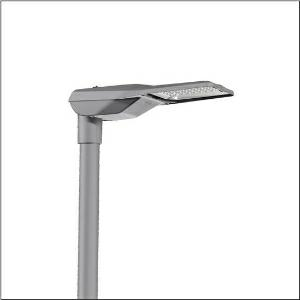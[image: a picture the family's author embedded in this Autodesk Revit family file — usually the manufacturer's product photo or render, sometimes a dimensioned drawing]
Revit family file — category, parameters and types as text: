
# Revit family: streetlight_sl_21_iq_mini___st1_0ab_5xe2m31v08jb_8772
name_source: partatom
category: Lighting Fixtures
units: mm (PartAtom-declared; Revit-internal decimal feet)

## family parameters
Cut with Voids When Loaded = No
Host = Face
Light Source = No
Part Type = Normal
Room Calculation Point = No
Round Connector Dimension = Use Diameter
Shared = No

## types (1)
- --- (1 x LED, 9870 lm, 72.5 W, 3000K)
    Apparent Load = 73 VA
    CIE Flux Codes = 40 74 97 100 100
    Color Rendering = 70
    Color Temperature = 3000K
    Default Elevation = 1800 mm
    Description = Streetlight SL 21 iQ mini, mast luminaire, primary light control with lens, of PMMA, primary optical cover: cover, of toughened safety glass, transparent, light distribution: ST1.0aB, light emission: direct distribution, primary light characteristic: asymmetric, installation type: post-top, side-entry, LED, High Power LED, rated luminous flux: 9.870lm, luminous efficacy: 136lm/W, light colour: 730, colour temperature: 3000K, control gear: iQ-Street Remote, D4i with power reduction, control: pre-setting: logarithmic dimming characteristic, Street-Remote, Auto-Match, Temp-Guard, Lumen-Switch, Night-Set, Smart-Wire, Light-Fading, Desk-Remote (wireless, voltage-free reading and setting of iQ features in the workshop via application-optimized NFC function/RFID function), optimised constant luminous flux control (CLO 2.0), mains connection: 220..240V, AC, 50/60Hz, start of lifetime: 73W, end of service life: 76W, reduction: 33W, luminaire housing, of diecast aluminium, powder-coated, Siteco® metallic grey (DB 702S), corrosivity category C5 mid according to DIN EN ISO 12944, please order mast flange separately, inclination adjustable: 0°, 5°, 10°, 15°, sealing non-destructively replaceable, multi-level sealing system, length: 628mm, width: 235mm, height: 110mm, mast flange for spigot size: 42mm (side-entry): 5XC10008XM4, 60/48mm (side-entry/post-top): 5XC10108XM2, 76/60mm (side-entry/post-top): 5XC10108XM1, mounting height: 4..8m, Smart Interface above, protection rating (complete): IP66, insulation class (complete): insulation class II (safety insulation), certification: CE, ENEC, ENEC+, VDE, impact resistance: IK10, permissible operating ambient temperature for outdoor applications: -40..+50°C, standard-compliant lighting for roads and squares, packaging unit: 1 piece

Light Distribution: ST1.0aB
    Height = 110 mm
    Lamp = 1 x LED
    Lamp Light Flux = 9870 lm
    Lamp Power = 72.5 W
    Lamp count = 1
    Length = 625 mm
    Luminous efficacy = 136 lm/W
    Manufacturer = Siteco
    ModVariant = No
    Model = 5XE2M31V08JB
    Number of Poles = 1
    OnlyDefault = Yes
    Power Factor = 1
    Product Name = Streetlight SL 21 iQ mini | ST1.0aB
    Product group = mast luminaire | pylon top
    ProductGroupID = 6100
    Protection Class = Protection class II
    Protection Degree = IP 66
    RLX_Detail_Level = 1
    RLX_Emergency_Light_Flux = 0 lm
    RLX_Emergency_Type = 0
    RLX_Emergency_Type_DB = No
    RlxData = <blob elided: 26433 chars, md5=5cc03561>
    Socket = socket
    Standby Power = 0 W
    System Light Flux = 9870 lm
    System Power = 73 W
    Type Comments = factory setting: luminous flux: 100 % | dim-lin: 254 | 755 mA
    Type Image = l_1003515.jpg
    URL = http://relux.com
    VarID = @adj_112210
    Voltage = 0 V
    Weight = 0.00 kg
    Width = 234 mm

## geometry (parser evidence)
native form markers: Blend x4, Sweep x10
no freeform markers — native parametric forms only
